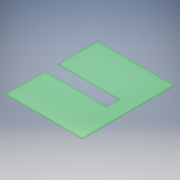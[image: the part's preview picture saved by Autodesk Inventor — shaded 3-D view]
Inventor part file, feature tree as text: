
AUTODESK INVENTOR PART (.ipt)
format: ipt  version: 2019 (Build 230136000, 136)  size: 115,712 bytes
history: native  units: in
note: dims shown in document units (in); Inventor stores cm internally (conversion verified against a paired STEP export)
features: extrude x1, sketch x1
ambient origin geometry x8: Origin, YZ Plane, XZ Plane, XY Plane, X Axis, Y Axis, Z Axis, Center Point
bodies: Solid1 (feature_tree)
feature tree (2):
  extrude  "Extrusion1"  Depth=5.0in
  sketch  "Sketch1"  dims[d0=6.0in d1=5.0in d2=0.85in d3=2.575in d4=4.0in d5=0.073in d6=0.0in]
